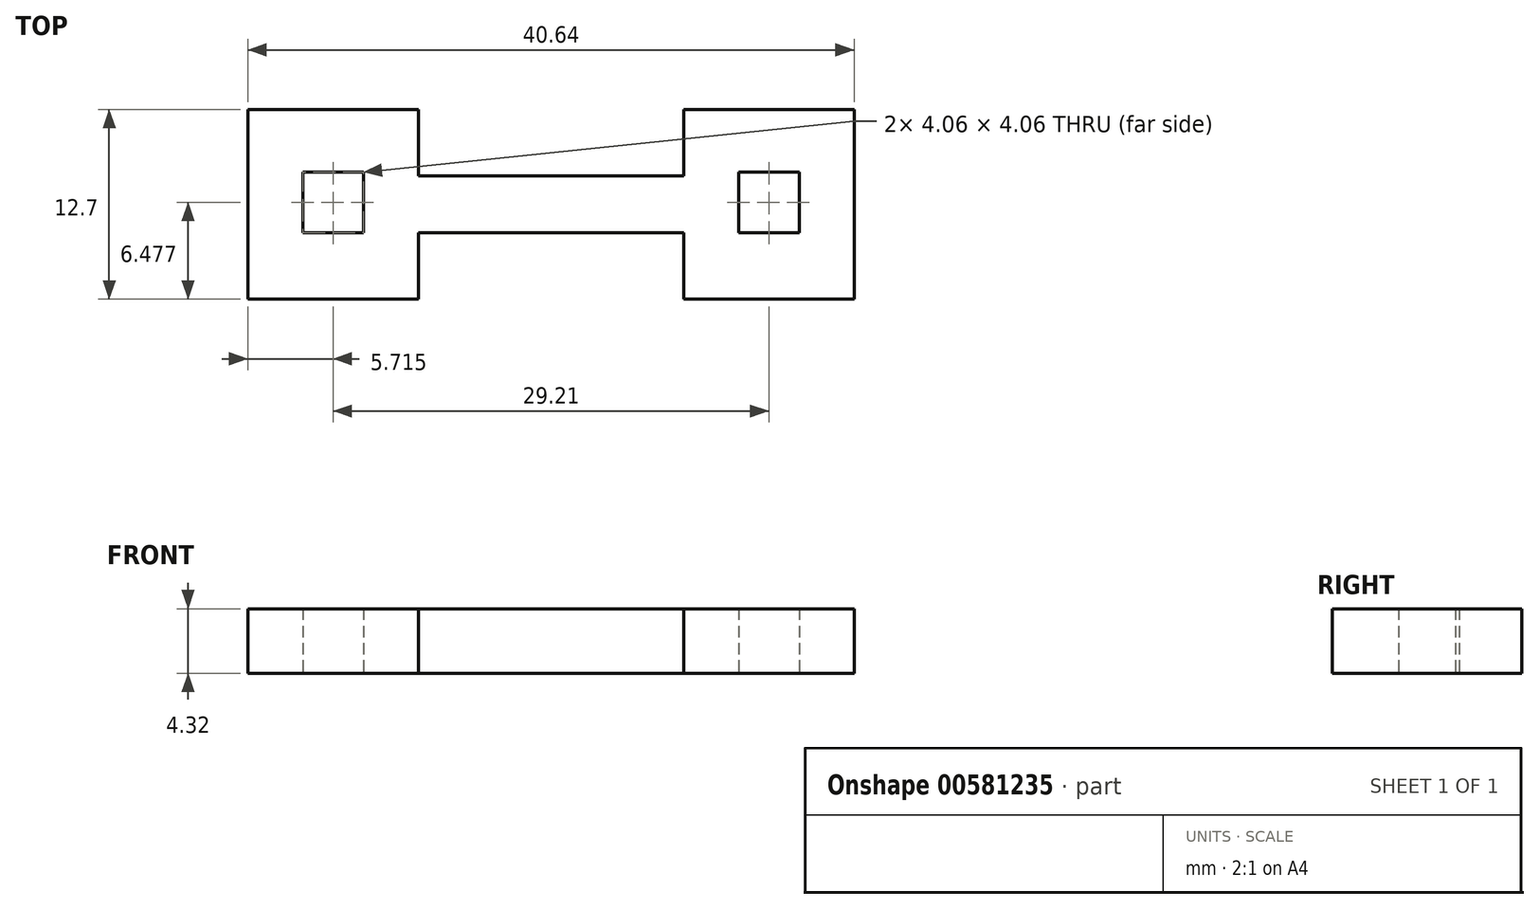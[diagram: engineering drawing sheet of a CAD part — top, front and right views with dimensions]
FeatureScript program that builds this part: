
annotation { "Feature Type Name" : "Feature", "Feature Type Description" : "" }
export const myFeature = defineFeature(function(context is Context, id is Id, definition is map)
    precondition{}
    {
        {
            var Q0;
            Q0=qCreatedBy(makeId("Top.planeOp"),FACE);
            var sketch = newSketch(context, id + "F0", { "sketchPlane" : qUnion([Q0])});
            skLineSegment(sketch, "E0.bottom", {"start": v(8.9, -1.9) * mm, "end": v(-8.89, -1.9) * mm});
            skLineSegment(sketch, "E0.top", {"start": v(8.9, 1.9) * mm, "end": v(-8.89, 1.9) * mm});
            skLineSegment(sketch, "E0.right", {"start": v(-8.89, -1.9) * mm, "end": v(-8.89, 1.9) * mm});
            skPoint(sketch, "E0.middle", {"position": v(0, 0) * mm});
            skLineSegment(sketch, "E1.bottom", {"start": v(8.9, -6.35) * mm, "end": v(20.32, -6.35) * mm});
            skLineSegment(sketch, "E1.top", {"start": v(8.9, 6.35) * mm, "end": v(20.32, 6.35) * mm});
            skLineSegment(sketch, "E1.left", {"start": v(8.9, -6.35) * mm, "end": v(8.9, -1.9) * mm});
            skLineSegment(sketch, "E1.right", {"start": v(20.32, -6.35) * mm, "end": v(20.32, 6.35) * mm});
            skLineSegment(sketch, "E2.bottom", {"start": v(12.57, 2.16) * mm, "end": v(16.64, 2.16) * mm});
            skLineSegment(sketch, "E2.top", {"start": v(12.57, -1.9) * mm, "end": v(16.64, -1.9) * mm});
            skLineSegment(sketch, "E2.left", {"start": v(12.57, 2.16) * mm, "end": v(12.57, -1.9) * mm});
            skLineSegment(sketch, "E2.right", {"start": v(16.64, 2.16) * mm, "end": v(16.64, -1.9) * mm});
            skLineSegment(sketch, "E3.MirrorCS", {"start": v(-8.9, -6.35) * mm, "end": v(-8.9, -1.9) * mm});
            skLineSegment(sketch, "E4.MirrorCS", {"start": v(-8.9, 6.35) * mm, "end": v(-20.32, 6.35) * mm});
            skLineSegment(sketch, "E5.MirrorCS", {"start": v(-20.32, -6.35) * mm, "end": v(-20.32, 6.35) * mm});
            skLineSegment(sketch, "E6.MirrorCS", {"start": v(-8.9, -6.35) * mm, "end": v(-20.32, -6.35) * mm});
            skLineSegment(sketch, "E7.MirrorCS", {"start": v(-12.57, -1.9) * mm, "end": v(-16.64, -1.9) * mm});
            skLineSegment(sketch, "E8.MirrorCS", {"start": v(-12.57, 2.16) * mm, "end": v(-12.57, -1.9) * mm});
            skLineSegment(sketch, "E9.MirrorCS", {"start": v(-12.57, 2.16) * mm, "end": v(-16.64, 2.16) * mm});
            skLineSegment(sketch, "E10.MirrorCS", {"start": v(-16.64, 2.16) * mm, "end": v(-16.64, -1.9) * mm});
            skLineSegment(sketch, "E11.trimOffspring", {"start": v(-8.9, 1.9) * mm, "end": v(-8.9, 6.35) * mm});
            skLineSegment(sketch, "E12.trimOffspring", {"start": v(8.9, 1.9) * mm, "end": v(8.9, 6.35) * mm});
            skSolve(sketch);
        }
        {
            var Q0;
            Q0 = qSketchRegion(id + "F0", true);
            extrude(context, id + "F1", {"entities" : qUnion([Q0]), "depth" : 4.32 * mm, "offsetDistance" : 25.4 * mm});
        }
    });
